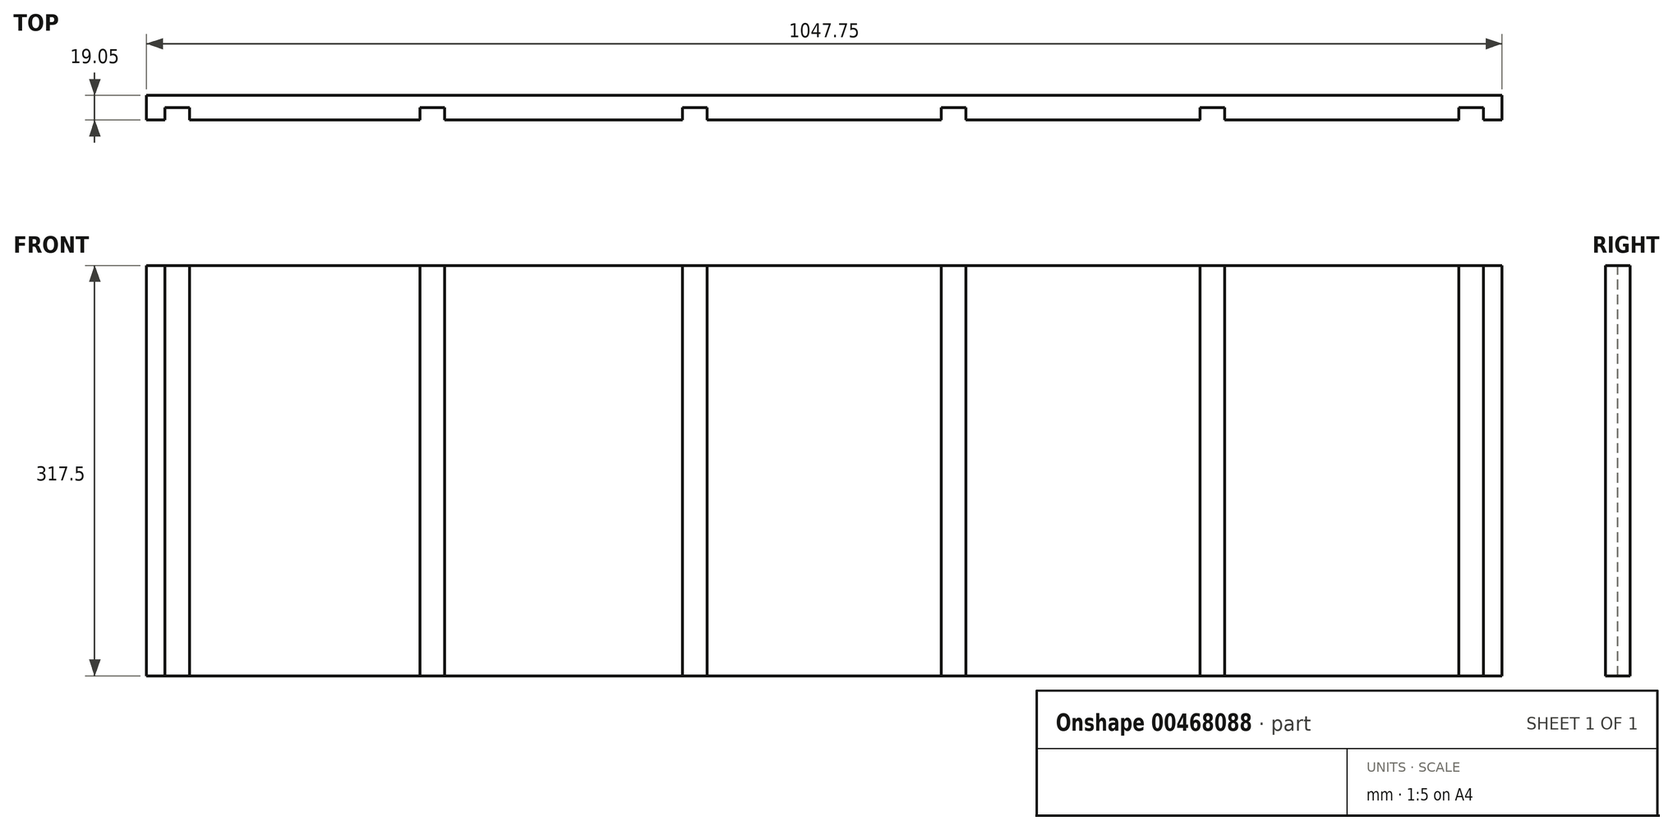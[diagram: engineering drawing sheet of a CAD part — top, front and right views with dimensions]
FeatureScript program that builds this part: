
annotation { "Feature Type Name" : "Feature", "Feature Type Description" : "" }
export const myFeature = defineFeature(function(context is Context, id is Id, definition is map)
    precondition{}
    {
        {
            var Q0;
            Q0=qCreatedBy(makeId("Front.planeOp"),FACE);
            var sketch = newSketch(context, id + "F0", { "sketchPlane" : qUnion([Q0])});
            skLineSegment(sketch, "E0.bottom", {"start": v(0, 0) * mm, "end": v(1047.75, 0) * mm});
            skLineSegment(sketch, "E0.top", {"start": v(0, 317.5) * mm, "end": v(1047.75, 317.5) * mm});
            skLineSegment(sketch, "E0.left", {"start": v(0, 0) * mm, "end": v(0, 317.5) * mm});
            skLineSegment(sketch, "E0.right", {"start": v(1047.75, 0) * mm, "end": v(1047.75, 317.5) * mm});
            skSolve(sketch);
        }
        {
            var Q0;
            Q0=makeQuery(id+"F0.imprint","IMPRINT",FACE,{"disambiguationData":[TD([[makeQuery(id+"F0.imprint","IMPRINT",EDGE,{"derivedFrom":sQuery(id+"F0.wireOp",EDGE,"E0.bottom")}),1.0]])]});
            extrude(context, id + "F1", {"entities" : qUnion([Q0]), "depth" : 19.05 * mm});
        }
        {
            var Q0;
            Q0=makeQuery(id+"F1.opExtrude","CAP_FACE",FACE,{"disambiguationData":[OSD([sQuery(id+"F0.wireOp",EDGE,"E0.bottom"),sQuery(id+"F0.wireOp",EDGE,"E0.top"),sQuery(id+"F0.wireOp",EDGE,"E0.left"),sQuery(id+"F0.wireOp",EDGE,"E0.right")])],"isStart":false});
            var sketch = newSketch(context, id + "F2", { "sketchPlane" : qUnion([Q0])});
            skLineSegment(sketch, "E1.bottom", {"start": v(14.08, 0) * mm, "end": v(33.13, 0) * mm});
            skLineSegment(sketch, "E1.top", {"start": v(14.08, 317.5) * mm, "end": v(33.13, 317.5) * mm});
            skLineSegment(sketch, "E1.left", {"start": v(14.08, 0) * mm, "end": v(14.08, 317.5) * mm});
            skLineSegment(sketch, "E1.right", {"start": v(33.13, 0) * mm, "end": v(33.13, 317.5) * mm});
            skSolve(sketch);
        }
        {
            var Q0;
            Q0=makeQuery(id+"F2.imprint","IMPRINT",FACE,{"disambiguationData":[TD([[makeQuery(id+"F2.imprint","IMPRINT",EDGE,{"derivedFrom":sQuery(id+"F2.wireOp",EDGE,"E1.bottom")}),1.0]])]});
            extrude(context, id + "F3", {"entities" : qUnion([Q0]), "operationType" : NewBodyOperationType.REMOVE, "oppositeDirection" : true, "depth" : 9.52 * mm});
        }
        {
            var Q0;
            {var subQ0=sQuery(id+"F0.wireOp",EDGE,"E0.bottom");var subQ1=sQuery(id+"F0.wireOp",EDGE,"E0.right");var subQ2=sQuery(id+"F0.wireOp",EDGE,"E0.top");Q0=makeQuery(id+"F3.boolean.opBoolean","SPLIT",FACE,{"disambiguationData":[TD([makeQuery(id+"F1.opExtrude","SWEPT_FACE",FACE,{"disambiguationData":[OSD([subQ1])]})])],"derivedFrom":makeQuery(id+"F1.opExtrude","CAP_FACE",FACE,{"disambiguationData":[OSD([subQ0,subQ2,sQuery(id+"F0.wireOp",EDGE,"E0.left"),subQ1])],"isStart":false})});}
            var sketch = newSketch(context, id + "F4", { "sketchPlane" : qUnion([Q0])});
            skLineSegment(sketch, "E2.bottom", {"start": v(1033.46, 0) * mm, "end": v(1014.41, 0) * mm});
            skLineSegment(sketch, "E2.top", {"start": v(1033.46, 317.5) * mm, "end": v(1014.41, 317.5) * mm});
            skLineSegment(sketch, "E2.left", {"start": v(1033.46, 0) * mm, "end": v(1033.46, 317.5) * mm});
            skLineSegment(sketch, "E2.right", {"start": v(1014.41, 0) * mm, "end": v(1014.41, 317.5) * mm});
            skSolve(sketch);
        }
        {
            var Q0;
            Q0=makeQuery(id+"F4.imprint","IMPRINT",FACE,{"disambiguationData":[TD([[makeQuery(id+"F4.imprint","IMPRINT",EDGE,{"derivedFrom":sQuery(id+"F4.wireOp",EDGE,"E2.bottom")}),1.0]])]});
            extrude(context, id + "F5", {"entities" : qUnion([Q0]), "operationType" : NewBodyOperationType.REMOVE, "oppositeDirection" : true, "depth" : 9.52 * mm});
        }
        {
            var Q0;
            {var subQ0=sQuery(id+"F0.wireOp",EDGE,"E0.bottom");var subQ2=sQuery(id+"F0.wireOp",EDGE,"E0.top");var subQ4=makeQuery(id+"F3.opExtrude","SWEPT_FACE",FACE,{"disambiguationData":[OSD([sQuery(id+"F2.wireOp",EDGE,"E1.right")])]});var subQ5=sQuery(id+"F0.wireOp",EDGE,"E0.right");Q0=makeQuery(id+"F5.boolean.opBoolean","SPLIT",FACE,{"disambiguationData":[TD([makeQuery(id+"F3.boolean.opBoolean","COPY",FACE,{"derivedFrom":subQ4})])],"derivedFrom":makeQuery(id+"F3.boolean.opBoolean","SPLIT",FACE,{"disambiguationData":[TD([makeQuery(id+"F1.opExtrude","SWEPT_FACE",FACE,{"disambiguationData":[OSD([subQ5])]})])],"derivedFrom":makeQuery(id+"F1.opExtrude","CAP_FACE",FACE,{"disambiguationData":[OSD([subQ0,subQ2,sQuery(id+"F0.wireOp",EDGE,"E0.left"),subQ5])],"isStart":false})})});}
            var sketch = newSketch(context, id + "F6", { "sketchPlane" : qUnion([Q0])});
            skLineSegment(sketch, "E3.bottom", {"start": v(814.39, 317.5) * mm, "end": v(833.44, 317.5) * mm});
            skLineSegment(sketch, "E3.top", {"start": v(814.39, 0) * mm, "end": v(833.44, 0) * mm});
            skLineSegment(sketch, "E3.left", {"start": v(814.39, 317.5) * mm, "end": v(814.39, 0) * mm});
            skLineSegment(sketch, "E3.right", {"start": v(833.44, 317.5) * mm, "end": v(833.44, 0) * mm});
            skSolve(sketch);
        }
        {
            var Q0;
            Q0=makeQuery(id+"F6.imprint","IMPRINT",FACE,{"disambiguationData":[TD([[makeQuery(id+"F6.imprint","IMPRINT",EDGE,{"derivedFrom":sQuery(id+"F6.wireOp",EDGE,"E3.bottom")}),-1.0]])]});
            extrude(context, id + "F7", {"entities" : qUnion([Q0]), "operationType" : NewBodyOperationType.REMOVE, "oppositeDirection" : true, "depth" : 9.52 * mm});
        }
        {
            var Q0;
            {var subQ0=sQuery(id+"F0.wireOp",EDGE,"E0.bottom");var subQ2=sQuery(id+"F0.wireOp",EDGE,"E0.top");var subQ4=makeQuery(id+"F3.opExtrude","SWEPT_FACE",FACE,{"disambiguationData":[OSD([sQuery(id+"F2.wireOp",EDGE,"E1.right")])]});var subQ5=makeQuery(id+"F3.boolean.opBoolean","COPY",FACE,{"derivedFrom":subQ4});var subQ6=sQuery(id+"F0.wireOp",EDGE,"E0.right");Q0=makeQuery(id+"F7.boolean.opBoolean","SPLIT",FACE,{"disambiguationData":[TD([subQ5])],"derivedFrom":makeQuery(id+"F5.boolean.opBoolean","SPLIT",FACE,{"disambiguationData":[TD([subQ5])],"derivedFrom":makeQuery(id+"F3.boolean.opBoolean","SPLIT",FACE,{"disambiguationData":[TD([makeQuery(id+"F1.opExtrude","SWEPT_FACE",FACE,{"disambiguationData":[OSD([subQ6])]})])],"derivedFrom":makeQuery(id+"F1.opExtrude","CAP_FACE",FACE,{"disambiguationData":[OSD([subQ0,subQ2,sQuery(id+"F0.wireOp",EDGE,"E0.left"),subQ6])],"isStart":false})})})});}
            var sketch = newSketch(context, id + "F8", { "sketchPlane" : qUnion([Q0])});
            skLineSegment(sketch, "E4.bottom", {"start": v(211.46, 317.5) * mm, "end": v(230.5, 317.5) * mm});
            skLineSegment(sketch, "E4.top", {"start": v(211.46, 0) * mm, "end": v(230.5, 0) * mm});
            skLineSegment(sketch, "E4.left", {"start": v(211.46, 317.5) * mm, "end": v(211.46, 0) * mm});
            skLineSegment(sketch, "E4.right", {"start": v(230.5, 317.5) * mm, "end": v(230.5, 0) * mm});
            skSolve(sketch);
        }
        {
            var Q0;
            Q0=makeQuery(id+"F8.imprint","IMPRINT",FACE,{"disambiguationData":[TD([[makeQuery(id+"F8.imprint","IMPRINT",EDGE,{"derivedFrom":sQuery(id+"F8.wireOp",EDGE,"E4.bottom")}),-1.0]])]});
            extrude(context, id + "F9", {"entities" : qUnion([Q0]), "operationType" : NewBodyOperationType.REMOVE, "oppositeDirection" : true, "depth" : 9.52 * mm});
        }
        {
            var Q0;
            {var subQ0=sQuery(id+"F0.wireOp",EDGE,"E0.bottom");var subQ2=sQuery(id+"F0.wireOp",EDGE,"E0.top");var subQ4=makeQuery(id+"F7.opExtrude","SWEPT_FACE",FACE,{"disambiguationData":[OSD([sQuery(id+"F6.wireOp",EDGE,"E3.left")])]});var subQ5=makeQuery(id+"F3.opExtrude","SWEPT_FACE",FACE,{"disambiguationData":[OSD([sQuery(id+"F2.wireOp",EDGE,"E1.right")])]});var subQ6=makeQuery(id+"F3.boolean.opBoolean","COPY",FACE,{"derivedFrom":subQ5});var subQ7=sQuery(id+"F0.wireOp",EDGE,"E0.right");Q0=makeQuery(id+"F9.boolean.opBoolean","SPLIT",FACE,{"disambiguationData":[TD([makeQuery(id+"F7.boolean.opBoolean","COPY",FACE,{"derivedFrom":subQ4})])],"derivedFrom":makeQuery(id+"F7.boolean.opBoolean","SPLIT",FACE,{"disambiguationData":[TD([subQ6])],"derivedFrom":makeQuery(id+"F5.boolean.opBoolean","SPLIT",FACE,{"disambiguationData":[TD([subQ6])],"derivedFrom":makeQuery(id+"F3.boolean.opBoolean","SPLIT",FACE,{"disambiguationData":[TD([makeQuery(id+"F1.opExtrude","SWEPT_FACE",FACE,{"disambiguationData":[OSD([subQ7])]})])],"derivedFrom":makeQuery(id+"F1.opExtrude","CAP_FACE",FACE,{"disambiguationData":[OSD([subQ0,subQ2,sQuery(id+"F0.wireOp",EDGE,"E0.left"),subQ7])],"isStart":false})})})})});}
            var sketch = newSketch(context, id + "F10", { "sketchPlane" : qUnion([Q0])});
            skLineSegment(sketch, "E5.bottom", {"start": v(414.34, 317.5) * mm, "end": v(433.39, 317.5) * mm});
            skLineSegment(sketch, "E5.top", {"start": v(414.34, 0) * mm, "end": v(433.39, 0) * mm});
            skLineSegment(sketch, "E5.left", {"start": v(414.34, 317.5) * mm, "end": v(414.34, 0) * mm});
            skLineSegment(sketch, "E5.right", {"start": v(433.39, 317.5) * mm, "end": v(433.39, 0) * mm});
            skSolve(sketch);
        }
        {
            var Q0;
            Q0 = qSketchRegion(id + "F10", true);
            extrude(context, id + "F11", {"entities" : qUnion([Q0]), "operationType" : NewBodyOperationType.REMOVE, "oppositeDirection" : true, "depth" : 9.52 * mm});
        }
        {
            var Q0;
            {var subQ0=sQuery(id+"F0.wireOp",EDGE,"E0.bottom");var subQ2=sQuery(id+"F0.wireOp",EDGE,"E0.top");var subQ4=makeQuery(id+"F7.opExtrude","SWEPT_FACE",FACE,{"disambiguationData":[OSD([sQuery(id+"F6.wireOp",EDGE,"E3.left")])]});var subQ5=makeQuery(id+"F7.boolean.opBoolean","COPY",FACE,{"derivedFrom":subQ4});var subQ6=makeQuery(id+"F3.opExtrude","SWEPT_FACE",FACE,{"disambiguationData":[OSD([sQuery(id+"F2.wireOp",EDGE,"E1.right")])]});var subQ7=makeQuery(id+"F3.boolean.opBoolean","COPY",FACE,{"derivedFrom":subQ6});var subQ8=sQuery(id+"F0.wireOp",EDGE,"E0.right");Q0=makeQuery(id+"F11.boolean.opBoolean","SPLIT",FACE,{"disambiguationData":[TD([subQ5])],"derivedFrom":makeQuery(id+"F9.boolean.opBoolean","SPLIT",FACE,{"disambiguationData":[TD([subQ5])],"derivedFrom":makeQuery(id+"F7.boolean.opBoolean","SPLIT",FACE,{"disambiguationData":[TD([subQ7])],"derivedFrom":makeQuery(id+"F5.boolean.opBoolean","SPLIT",FACE,{"disambiguationData":[TD([subQ7])],"derivedFrom":makeQuery(id+"F3.boolean.opBoolean","SPLIT",FACE,{"disambiguationData":[TD([makeQuery(id+"F1.opExtrude","SWEPT_FACE",FACE,{"disambiguationData":[OSD([subQ8])]})])],"derivedFrom":makeQuery(id+"F1.opExtrude","CAP_FACE",FACE,{"disambiguationData":[OSD([subQ0,subQ2,sQuery(id+"F0.wireOp",EDGE,"E0.left"),subQ8])],"isStart":false})})})})})});}
            var sketch = newSketch(context, id + "F12", { "sketchPlane" : qUnion([Q0])});
            skLineSegment(sketch, "E6.bottom", {"start": v(614.36, 317.5) * mm, "end": v(633.41, 317.5) * mm});
            skLineSegment(sketch, "E6.top", {"start": v(614.36, 0) * mm, "end": v(633.41, 0) * mm});
            skLineSegment(sketch, "E6.left", {"start": v(614.36, 317.5) * mm, "end": v(614.36, 0) * mm});
            skLineSegment(sketch, "E6.right", {"start": v(633.41, 317.5) * mm, "end": v(633.41, 0) * mm});
            skSolve(sketch);
        }
        {
            var Q0;
            Q0=makeQuery(id+"F12.imprint","IMPRINT",FACE,{"disambiguationData":[TD([[makeQuery(id+"F12.imprint","IMPRINT",EDGE,{"derivedFrom":sQuery(id+"F12.wireOp",EDGE,"E6.bottom")}),-1.0]])]});
            extrude(context, id + "F13", {"entities" : qUnion([Q0]), "operationType" : NewBodyOperationType.REMOVE, "oppositeDirection" : true, "depth" : 9.52 * mm});
        }
    });
